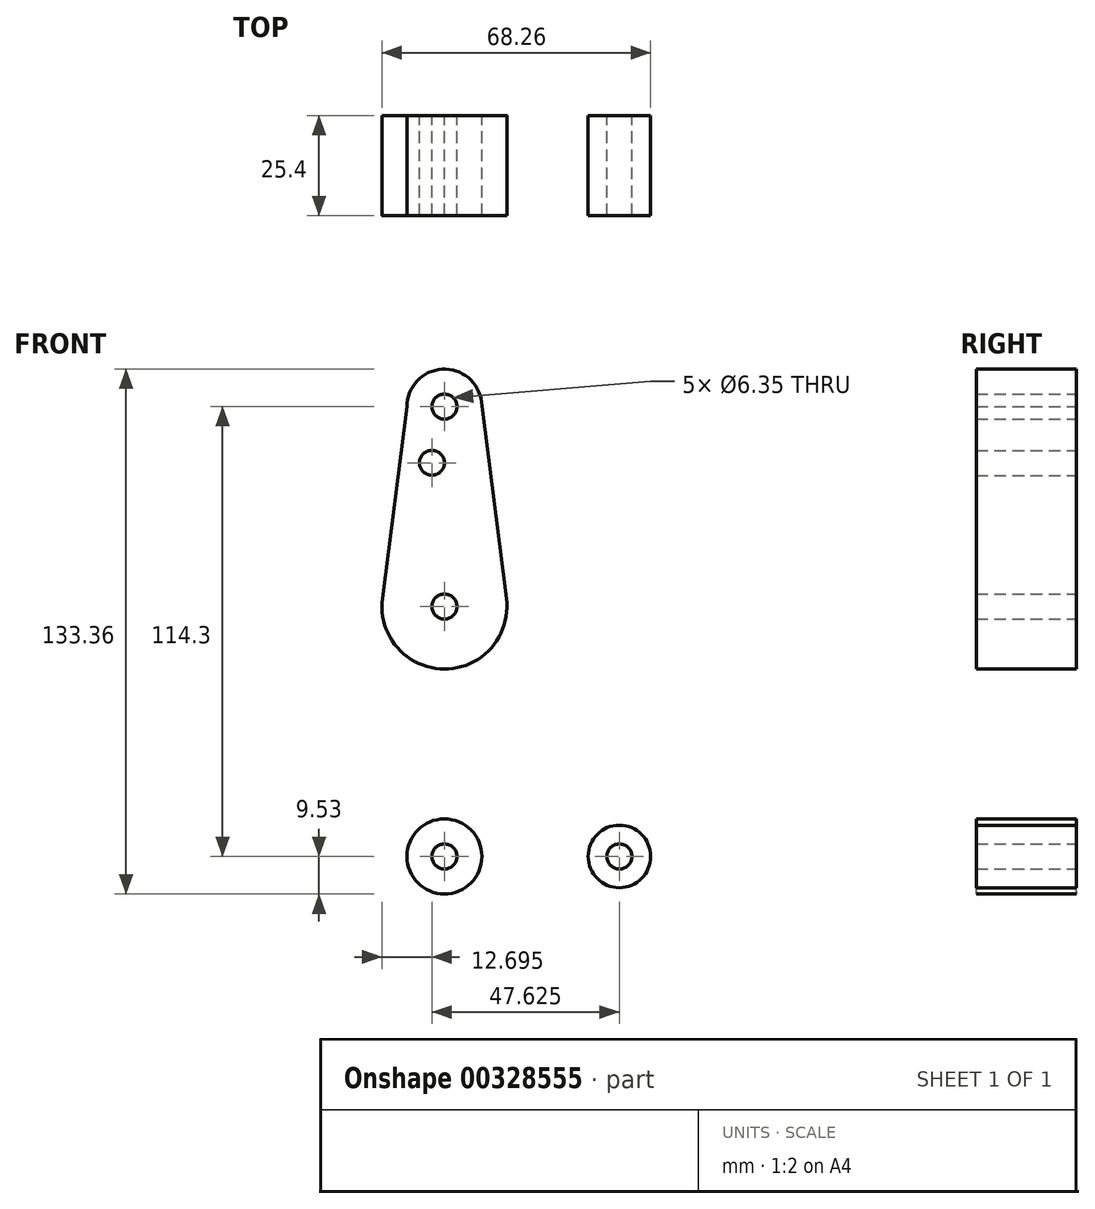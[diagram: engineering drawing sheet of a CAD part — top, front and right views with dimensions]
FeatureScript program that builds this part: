
annotation { "Feature Type Name" : "Feature", "Feature Type Description" : "" }
export const myFeature = defineFeature(function(context is Context, id is Id, definition is map)
    precondition{}
    {
        {
            var Q0;
            Q0=qCreatedBy(makeId("Front.planeOp"),FACE);
            var sketch = newSketch(context, id + "F0", { "sketchPlane" : qUnion([Q0])});
            skLineSegment(sketch, "E0", {"start": v(0, 0) * mm, "end": v(44.45, 0) * mm, "construction": true});
            skLineSegment(sketch, "E1", {"start": v(0, 0) * mm, "end": v(0, 114.3) * mm, "construction": true});
            skCircle(sketch, "E2", {"center": v(0, 0) * mm, "radius": 9.53 * mm});
            skCircle(sketch, "E3", {"center": v(44.45, 0) * mm, "radius": 7.94 * mm});
            skCircle(sketch, "E4", {"center": v(0, 114.3) * mm, "radius": 9.53 * mm});
            skCircle(sketch, "E5", {"center": v(0, 63.5) * mm, "radius": 15.88 * mm});
            skLineSegment(sketch, "E6", {"start": v(-9.53, 114.3) * mm, "end": v(-15.75, 65.5) * mm});
            skLineSegment(sketch, "E7", {"start": v(0, -9.53) * mm, "end": v(44.73, -7.93) * mm});
            skLineSegment(sketch, "E8", {"start": v(18.97, 8.85) * mm, "end": v(44.73, 7.93) * mm});
            skLineSegment(sketch, "E9", {"start": v(9.45, 115.5) * mm, "end": v(15.75, 65.48) * mm});
            skCircle(sketch, "E10", {"center": v(0, 114.3) * mm, "radius": 3.18 * mm});
            skCircle(sketch, "E11", {"center": v(0, 0) * mm, "radius": 3.18 * mm});
            skCircle(sketch, "E12", {"center": v(44.45, 0) * mm, "radius": 3.18 * mm});
            skCircle(sketch, "E13", {"center": v(0, 63.5) * mm, "radius": 3.18 * mm});
            skCircle(sketch, "E14", {"center": v(-3.18, 100.03) * mm, "radius": 3.18 * mm});
            skPoint(sketch, "E15.newPointA", {"position": v(9.57, 0) * mm});
            skArc(sketch, "E15.filletArc", {"start": v(11.34, 17.6) * mm, "mid": v(13.26, 11.57) * mm, "end": v(18.97, 8.85) * mm});
            skLineSegment(sketch, "E16", {"start": v(-15.8, 61.91) * mm, "end": v(-9.57, 0) * mm});
            skLineSegment(sketch, "E17", {"start": v(15.8, 61.91) * mm, "end": v(11.34, 17.6) * mm});
            skSolve(sketch);
        }
        {
            var Q0;
            Q0 = qSketchRegion(id + "F0", true);
            extrude(context, id + "F1", {"entities" : qUnion([Q0]), "depth" : 25.4 * mm});
        }
    });
